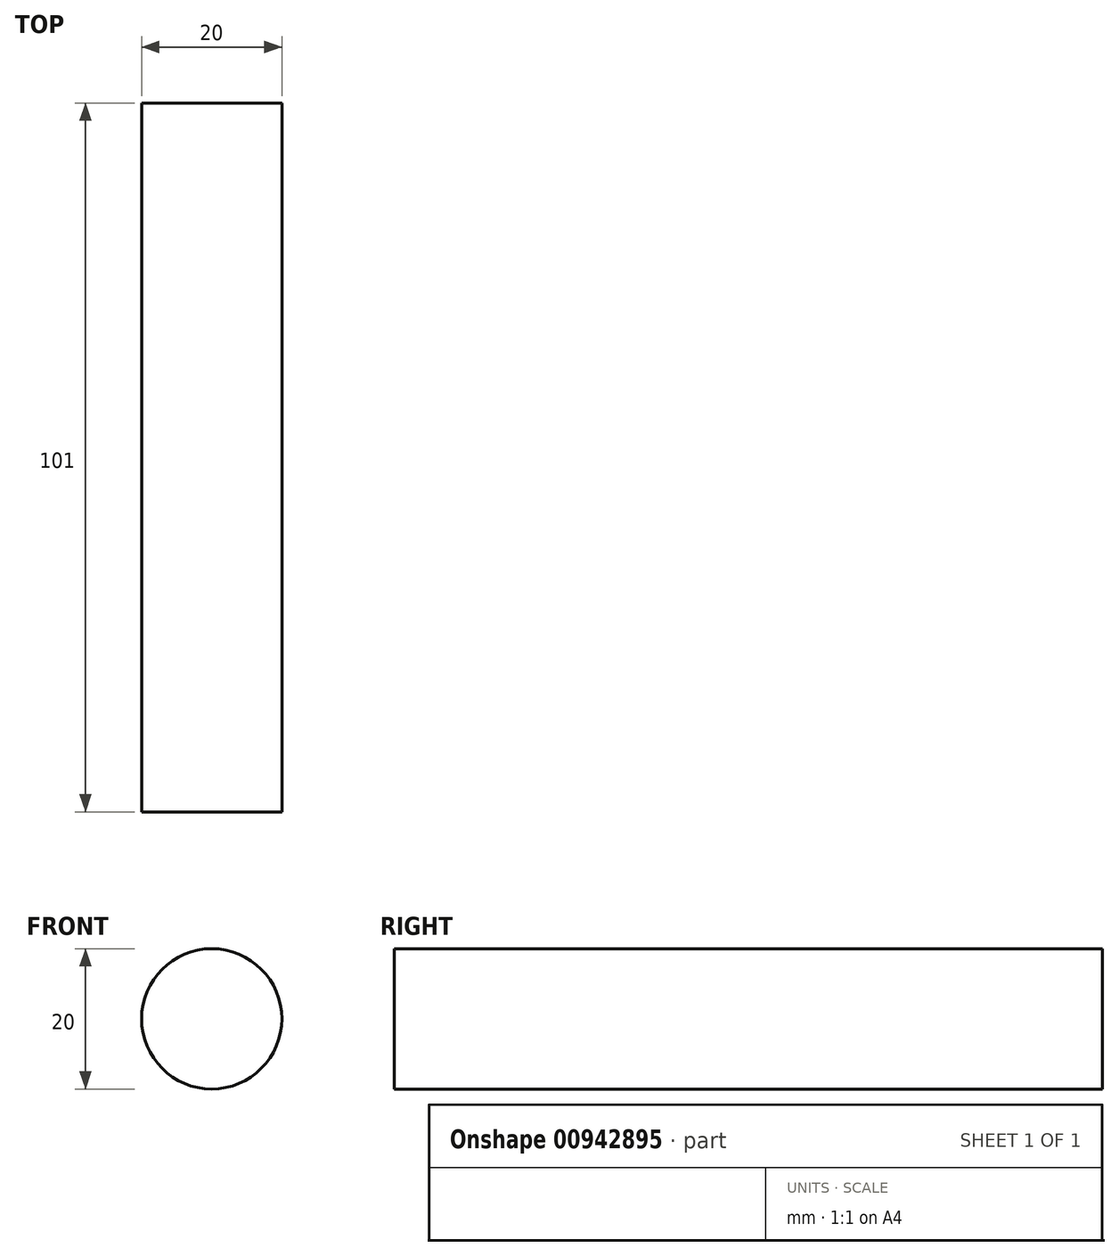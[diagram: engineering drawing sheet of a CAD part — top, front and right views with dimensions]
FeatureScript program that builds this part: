
annotation { "Feature Type Name" : "Feature", "Feature Type Description" : "" }
export const myFeature = defineFeature(function(context is Context, id is Id, definition is map)
    precondition{}
    {
        {
            var Q0;
            Q0=qCreatedBy(makeId("Front.planeOp"),FACE);
            var sketch = newSketch(context, id + "F0", { "sketchPlane" : qUnion([Q0])});
            skCircle(sketch, "E0", {"center": v(-40.68, 0) * mm, "radius": 10 * mm});
            skSolve(sketch);
        }
        {
            var Q0;
            Q0=makeQuery(id+"F0.imprint","IMPRINT",FACE,{"disambiguationData":[TD([[makeQuery(id+"F0.imprint","IMPRINT",EDGE,{"derivedFrom":sQuery(id+"F0.wireOp",EDGE,"E0")}),1.0]])]});
            extrude(context, id + "F1", {"entities" : qUnion([Q0]), "oppositeDirection" : true, "depth" : 101 * mm, "offsetDistance" : 25 * mm});
        }
    });
